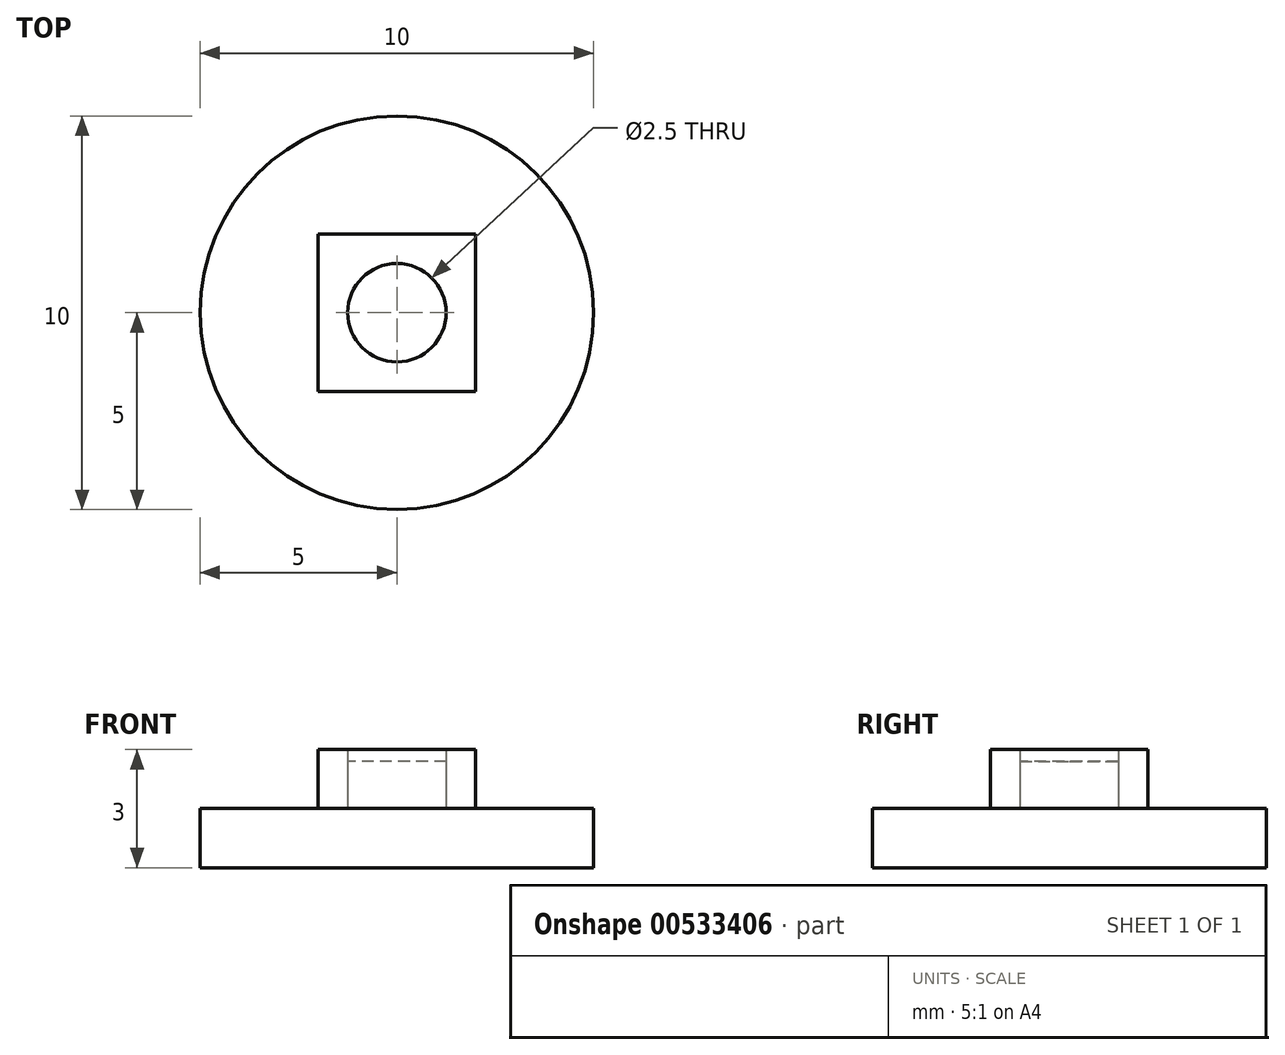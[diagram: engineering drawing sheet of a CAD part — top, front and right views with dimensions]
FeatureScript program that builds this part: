
annotation { "Feature Type Name" : "Feature", "Feature Type Description" : "" }
export const myFeature = defineFeature(function(context is Context, id is Id, definition is map)
    precondition{}
    {
        {
            var Q0;
            Q0=qCreatedBy(makeId("Top.planeOp"),FACE);
            var sketch = newSketch(context, id + "F0", { "sketchPlane" : qUnion([Q0])});
            skCircle(sketch, "E0", {"center": v(0, 0) * mm, "radius": 5 * mm});
            skLineSegment(sketch, "E1.bottom", {"start": v(2, -2) * mm, "end": v(-2, -2) * mm});
            skLineSegment(sketch, "E1.top", {"start": v(2, 2) * mm, "end": v(-2, 2) * mm});
            skLineSegment(sketch, "E1.left", {"start": v(2, -2) * mm, "end": v(2, 2) * mm});
            skLineSegment(sketch, "E1.right", {"start": v(-2, -2) * mm, "end": v(-2, 2) * mm});
            skCircle(sketch, "E2", {"center": v(0, 0) * mm, "radius": 1.25 * mm});
            skSolve(sketch);
        }
        {
            var Q0;
            Q0 = qSketchRegion(id + "F0", true);
            var Q1;
            Q1=makeQuery(id+"F0.imprint","IMPRINT",FACE,{"disambiguationData":[TD([[makeQuery(id+"F0.imprint","IMPRINT",EDGE,{"derivedFrom":sQuery(id+"F0.wireOp",EDGE,"E1.bottom")}),-1.0]])]});
            var Q2;
            Q2=makeQuery(id+"F0.imprint","IMPRINT",FACE,{"disambiguationData":[TD([[makeQuery(id+"F0.imprint","IMPRINT",EDGE,{"derivedFrom":sQuery(id+"F0.wireOp",EDGE,"E2")}),1.0]])]});
            extrude(context, id + "F1", {"entities" : qUnion([Q0, Q1, Q2]), "oppositeDirection" : true, "depth" : 1.5 * mm, "offsetDistance" : 25 * mm});
        }
        {
            var Q0;
            Q0=makeQuery(id+"F0.imprint","IMPRINT",FACE,{"disambiguationData":[TD([[makeQuery(id+"F0.imprint","IMPRINT",EDGE,{"derivedFrom":sQuery(id+"F0.wireOp",EDGE,"E1.bottom")}),-1.0]])]});
            extrude(context, id + "F2", {"entities" : qUnion([Q0]), "depth" : 1.5 * mm, "offsetDistance" : 25 * mm});
        }
        {
            var Q0;
            Q0=makeQuery(id+"F0.imprint","IMPRINT",FACE,{"disambiguationData":[TD([[makeQuery(id+"F0.imprint","IMPRINT",EDGE,{"derivedFrom":sQuery(id+"F0.wireOp",EDGE,"E2")}),1.0]])]});
            extrude(context, id + "F3", {"entities" : qUnion([Q0]), "depth" : 1.2 * mm, "offsetDistance" : 25 * mm});
        }
    });
